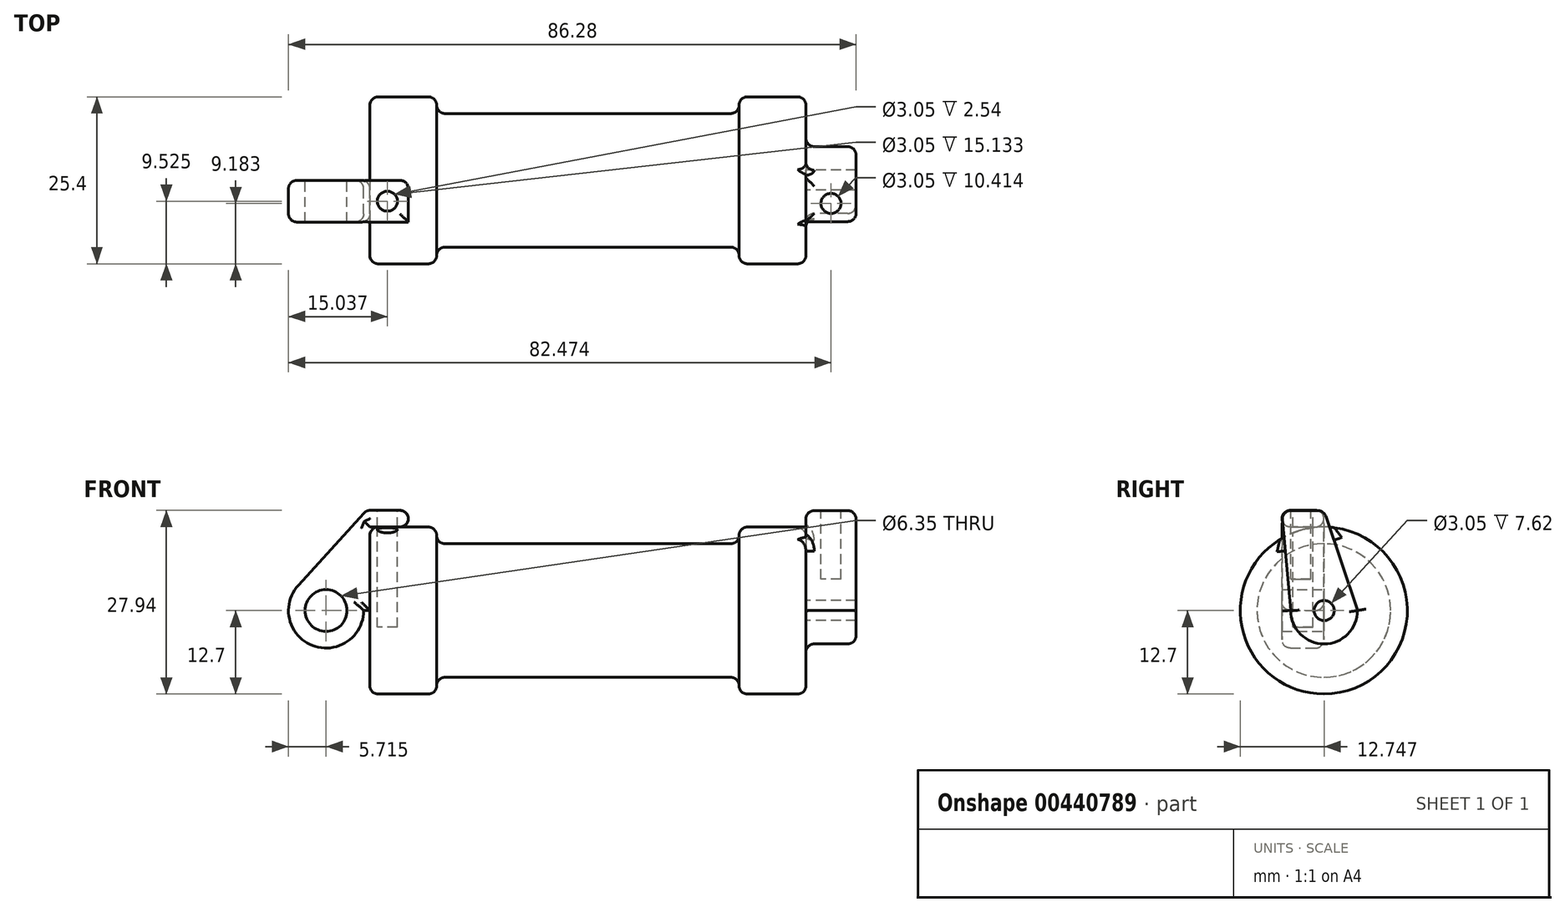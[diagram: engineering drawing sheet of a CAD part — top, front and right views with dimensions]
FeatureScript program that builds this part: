
annotation { "Feature Type Name" : "Feature", "Feature Type Description" : "" }
export const myFeature = defineFeature(function(context is Context, id is Id, definition is map)
    precondition{}
    {
        {
            var Q0;
            Q0=qCreatedBy(makeId("Front.planeOp"),FACE);
            var sketch = newSketch(context, id + "F0", { "sketchPlane" : qUnion([Q0])});
            skLineSegment(sketch, "E0", {"start": v(0, 0) * mm, "end": v(0, 12.7) * mm});
            skLineSegment(sketch, "E1", {"start": v(0, 12.7) * mm, "end": v(10.16, 12.7) * mm});
            skLineSegment(sketch, "E2", {"start": v(10.16, 12.7) * mm, "end": v(10.16, 10.16) * mm});
            skLineSegment(sketch, "E3", {"start": v(10.16, 10.16) * mm, "end": v(56.13, 10.16) * mm});
            skLineSegment(sketch, "E4", {"start": v(56.13, 10.16) * mm, "end": v(56.13, 12.7) * mm});
            skLineSegment(sketch, "E5", {"start": v(56.13, 12.7) * mm, "end": v(66.3, 12.7) * mm});
            skLineSegment(sketch, "E6", {"start": v(66.3, 12.7) * mm, "end": v(66.3, 0) * mm});
            skLineSegment(sketch, "E7", {"start": v(66.3, 0) * mm, "end": v(0, 0) * mm});
            skLineSegment(sketch, "E8", {"start": v(5.84, 15.24) * mm, "end": v(-0.5, 15.24) * mm});
            skLineSegment(sketch, "E9", {"start": v(-0.5, 15.24) * mm, "end": v(-10.88, 3.85) * mm});
            skLineSegment(sketch, "E10", {"start": v(0, 0) * mm, "end": v(-6.65, 0) * mm});
            skCircle(sketch, "E11", {"center": v(-6.65, 0) * mm, "radius": 5.72 * mm});
            skCircle(sketch, "E12", {"center": v(-6.65, 0) * mm, "radius": 3.18 * mm});
            skLineSegment(sketch, "E13", {"start": v(5.84, 15.24) * mm, "end": v(5.84, -9.4) * mm});
            skLineSegment(sketch, "E14", {"start": v(5.84, -9.4) * mm, "end": v(-8.18, -5.5) * mm});
            skSolve(sketch);
        }
        {
            var Q0;
            {var subQ0=sQuery(id+"F0.wireOp",EDGE,"E2");Q0=makeQuery(id+"F0.imprint","IMPRINT",FACE,{"disambiguationData":[TD([[makeQuery(id+"F0.imprint","IMPRINT",EDGE,{"derivedFrom":subQ0}),-1.0]])]});}
            var Q1;
            {var subQ0=sQuery(id+"F0.wireOp",EDGE,"E0");Q1=makeQuery(id+"F0.imprint","IMPRINT",FACE,{"disambiguationData":[TD([[makeQuery(id+"F0.imprint","IMPRINT",EDGE,{"derivedFrom":subQ0}),-1.0]])]});}
            var Q2;
            Q2=sQuery(id+"F0.wireOp",EDGE,"E7");
            revolve(context, id + "F1", {"entities" : qUnion([Q0, Q1]), "axis" : qUnion([Q2]), "revolveType" : RevolveType.FULL});
        }
        {
            var Q0;
            {var subQ1=sQuery(id+"F0.wireOp",EDGE,"E0");Q0=makeQuery(id+"F0.imprint","IMPRINT",FACE,{"disambiguationData":[TD([[makeQuery(id+"F0.imprint","IMPRINT",EDGE,{"derivedFrom":subQ1}),1.0]])]});}
            var Q1;
            {var subQ5=sQuery(id+"F0.wireOp",EDGE,"E12");Q1=makeQuery(id+"F0.imprint","IMPRINT",FACE,{"disambiguationData":[TD([[makeQuery(id+"F0.imprint","IMPRINT",EDGE,{"derivedFrom":subQ5}),-1.0]])]});}
            extrude(context, id + "F2", {"entities" : qUnion([Q0, Q1]), "depth" : 6.35 * mm});
        }
        {
            var Q0;
            Q0=makeQuery(id+"F1.opRevolve","SWEPT_FACE",FACE,{"disambiguationData":[OSD([sQuery(id+"F0.wireOp",EDGE,"E6")])]});
            var sketch = newSketch(context, id + "F3", { "sketchPlane" : qUnion([Q0])});
            skCircle(sketch, "E15", {"center": v(0.05, 0) * mm, "radius": 1.52 * mm});
            skCircle(sketch, "E16", {"center": v(0.05, 0) * mm, "radius": 5.08 * mm});
            skPoint(sketch, "E17", {"position": v(5.13, 0) * mm});
            skPoint(sketch, "E18", {"position": v(-5.03, 0) * mm});
            skLineSegment(sketch, "E19", {"start": v(-5.03, 0) * mm, "end": v(-6.4, 15.2) * mm});
            skLineSegment(sketch, "E20", {"start": v(-6.4, 15.2) * mm, "end": v(0.01, 15.2) * mm});
            skLineSegment(sketch, "E21", {"start": v(0.01, 15.2) * mm, "end": v(5.13, 0) * mm});
            skSolve(sketch);
        }
        {
            var Q0;
            {var subQ0=sQuery(id+"F3.wireOp",EDGE,"E19");var subQ1=sQuery(id+"F3.wireOp",EDGE,"E16");var subQ2=makeQuery(id+"F3.imprint","INTERSECT",VERTEX,{"derivedFrom":[subQ1,subQ0]});Q0=makeQuery(id+"F3.imprint","IMPRINT",FACE,{"disambiguationData":[TD([[makeQuery(id+"F3.imprint","IMPRINT",EDGE,{"disambiguationData":[TD([[subQ2,1.0]])],"derivedFrom":subQ1}),-1.0]])]});}
            var Q1;
            {var subQ0=sQuery(id+"F3.wireOp",EDGE,"E20");Q1=makeQuery(id+"F3.imprint","IMPRINT",FACE,{"disambiguationData":[TD([[makeQuery(id+"F3.imprint","IMPRINT",EDGE,{"derivedFrom":subQ0}),-1.0]])]});}
            var Q2;
            Q2=makeQuery(id+"F3.imprint","IMPRINT",FACE,{"disambiguationData":[TD([[makeQuery(id+"F3.imprint","IMPRINT",EDGE,{"derivedFrom":sQuery(id+"F3.wireOp",EDGE,"E15")}),-1.0]])]});
            extrude(context, id + "F4", {"entities" : qUnion([Q0, Q1, Q2]), "operationType" : NewBodyOperationType.ADD, "depth" : 7.62 * mm});
        }
        {
            var Q0;
            Q0=makeQuery(id+"F4.boolean.opBoolean","SPLIT",FACE,{"disambiguationData":[TD([makeQuery(id+"F4.opExtrude","SWEPT_FACE",FACE,{"disambiguationData":[OSD([sQuery(id+"F3.wireOp",EDGE,"E15")])]})])],"derivedFrom":makeQuery(id+"F1.opRevolve","SWEPT_FACE",FACE,{"disambiguationData":[OSD([sQuery(id+"F0.wireOp",EDGE,"E6")])]})});
            var Q1;
            Q1=makeQuery(id+"F1.opRevolve","SWEPT_FACE",FACE,{"disambiguationData":[OSD([sQuery(id+"F0.wireOp",EDGE,"E2")])]});
            extrude(context, id + "F5", {"entities" : qUnion([Q0]), "operationType" : NewBodyOperationType.ADD, "endBound" : BoundingType.UP_TO_SURFACE, "oppositeDirection" : true, "endBoundEntityFace" : qUnion([Q1]), "depth" : 25.4 * mm});
        }
        {
            var Q0;
            Q0=makeQuery(id+"F2.opExtrude","SWEPT_FACE",FACE,{"disambiguationData":[OSD([sQuery(id+"F0.wireOp",EDGE,"E8")])]});
            var sketch = newSketch(context, id + "F6", { "sketchPlane" : qUnion([Q0])});
            skCircle(sketch, "E22", {"center": v(2.67, -3.18) * mm, "radius": 1.52 * mm});
            skCircle(sketch, "E23", {"center": v(69.7, -3.25) * mm, "radius": 1.52 * mm});
            skPoint(sketch, "E24", {"position": v(2.67, 0) * mm});
            skPoint(sketch, "E25", {"position": v(2.67, -6.35) * mm});
            skPoint(sketch, "E26", {"position": v(69.67, -6.42) * mm});
            skPoint(sketch, "E27", {"position": v(69.72, -0.08) * mm});
            skSolve(sketch);
        }
        {
            var Q0;
            Q0=makeQuery(id+"F6.imprint","IMPRINT",FACE,{"disambiguationData":[TD([[makeQuery(id+"F6.imprint","IMPRINT",EDGE,{"derivedFrom":sQuery(id+"F6.wireOp",EDGE,"E22")}),1.0]])]});
            extrude(context, id + "F7", {"entities" : qUnion([Q0]), "operationType" : NewBodyOperationType.REMOVE, "oppositeDirection" : true, "depth" : 17.78 * mm});
        }
        {
            var Q0;
            Q0=makeQuery(id+"F4.opExtrude","SWEPT_FACE",FACE,{"disambiguationData":[OSD([sQuery(id+"F3.wireOp",EDGE,"E20")])]});
            var sketch = newSketch(context, id + "F8", { "sketchPlane" : qUnion([Q0])});
            skCircle(sketch, "E28", {"center": v(70.1, -3.52) * mm, "radius": 1.52 * mm});
            skPoint(sketch, "E29", {"position": v(70.1, -6.4) * mm});
            skLineSegment(sketch, "E30", {"start": v(70.1, -6.4) * mm, "end": v(70.1, 0.01) * mm});
            skSolve(sketch);
        }
        {
            var Q0;
            {var subQ0=sQuery(id+"F8.wireOp",EDGE,"E30");var subQ1=sQuery(id+"F8.wireOp",EDGE,"E28");var subQ2=makeQuery(id+"F8.imprint","INTERSECT",VERTEX,{"disambiguationData":[OD(0.0)],"derivedFrom":[subQ1,subQ0]});Q0=makeQuery(id+"F8.imprint","IMPRINT",FACE,{"disambiguationData":[TD([[makeQuery(id+"F8.imprint","IMPRINT",EDGE,{"disambiguationData":[TD([[subQ2,-1.0]])],"derivedFrom":subQ1}),1.0]])]});}
            var Q1;
            {var subQ0=sQuery(id+"F8.wireOp",EDGE,"E30");var subQ1=sQuery(id+"F8.wireOp",EDGE,"E28");var subQ2=makeQuery(id+"F8.imprint","INTERSECT",VERTEX,{"disambiguationData":[OD(0.0)],"derivedFrom":[subQ1,subQ0]});Q1=makeQuery(id+"F8.imprint","IMPRINT",FACE,{"disambiguationData":[TD([[makeQuery(id+"F8.imprint","IMPRINT",EDGE,{"disambiguationData":[TD([[subQ2,1.0]])],"derivedFrom":subQ1}),1.0]])]});}
            extrude(context, id + "F9", {"entities" : qUnion([Q0, Q1]), "operationType" : NewBodyOperationType.REMOVE, "oppositeDirection" : true, "depth" : 10.4 * mm});
        }
        {
            var Q0;
            {var subQ0=sQuery(id+"F0.wireOp",EDGE,"E5");var subQ1=sQuery(id+"F0.wireOp",EDGE,"E6");Q0=makeQuery(id+"F4.boolean.opBoolean","SPLIT",EDGE,{"disambiguationData":[topologyDisambiguationEdgeConnected([makeQuery(id+"F1.opRevolve","SWEPT_FACE",FACE,{"disambiguationData":[OSD([subQ1])]})])],"derivedFrom":makeQuery(id+"F1.opRevolve","SWEPT_EDGE",EDGE,{"disambiguationData":[OSD([subQ0,subQ1])]})});}
            var Q1;
            Q1=makeQuery(id+"F1.opRevolve","SWEPT_EDGE",EDGE,{"disambiguationData":[OSD([sQuery(id+"F0.wireOp",EDGE,"E4"),sQuery(id+"F0.wireOp",EDGE,"E5")])]});
            var Q2;
            Q2=makeQuery(id+"F1.opRevolve","SWEPT_EDGE",EDGE,{"disambiguationData":[OSD([sQuery(id+"F0.wireOp",EDGE,"E1"),sQuery(id+"F0.wireOp",EDGE,"E2")])]});
            var Q3;
            Q3=makeQuery(id+"F1.opRevolve","SWEPT_EDGE",EDGE,{"disambiguationData":[OSD([sQuery(id+"F0.wireOp",EDGE,"E0"),sQuery(id+"F0.wireOp",EDGE,"E1")])]});
            var Q4;
            Q4=makeQuery(id+"F1.opRevolve","SWEPT_EDGE",EDGE,{"disambiguationData":[OSD([sQuery(id+"F0.wireOp",EDGE,"E2"),sQuery(id+"F0.wireOp",EDGE,"E3")])]});
            var Q5;
            Q5=makeQuery(id+"F1.opRevolve","SWEPT_EDGE",EDGE,{"disambiguationData":[OSD([sQuery(id+"F0.wireOp",EDGE,"E3"),sQuery(id+"F0.wireOp",EDGE,"E4")])]});
            fillet(context, id + "F10", {"entities" : qUnion([Q0, Q1, Q2, Q3, Q4, Q5]), "radius" : 1.27 * mm, "tangentPropagation" : true, "allowEdgeOverflow" : false});
        }
        {
            var Q0;
            {var subQ0=sQuery(id+"F3.wireOp",EDGE,"E19");Q0=makeQuery(id+"F4.boolean.opBoolean","SPLIT",EDGE,{"disambiguationData":[topologyDisambiguationEdgeConnected([makeQuery(id+"F1.opRevolve","SWEPT_FACE",FACE,{"disambiguationData":[OSD([sQuery(id+"F0.wireOp",EDGE,"E6")])]})])],"derivedFrom":makeQuery(id+"F4.opExtrude","CAP_EDGE",EDGE,{"disambiguationData":[OSD([subQ0])],"isStart":true})});}
            var Q1;
            Q1=makeQuery(id+"F4.opExtrude","CAP_EDGE",EDGE,{"disambiguationData":[OSD([sQuery(id+"F3.wireOp",EDGE,"E16")])],"isStart":true});
            var Q2;
            Q2=makeQuery(id+"F4.opExtrude","SWEPT_EDGE",EDGE,{"disambiguationData":[OSD([sQuery(id+"F3.wireOp",EDGE,"E19"),sQuery(id+"F3.wireOp",EDGE,"E20")])]});
            var Q3;
            Q3=makeQuery(id+"F4.opExtrude","CAP_EDGE",EDGE,{"disambiguationData":[OSD([sQuery(id+"F3.wireOp",EDGE,"E20")])],"isStart":false});
            var Q4;
            Q4=makeQuery(id+"F4.opExtrude","CAP_EDGE",EDGE,{"disambiguationData":[OSD([sQuery(id+"F3.wireOp",EDGE,"E20")])],"isStart":true});
            var Q5;
            Q5=makeQuery(id+"F4.opExtrude","SWEPT_EDGE",EDGE,{"disambiguationData":[OSD([sQuery(id+"F3.wireOp",EDGE,"E20"),sQuery(id+"F3.wireOp",EDGE,"E21")])]});
            var Q6;
            {var subQ0=sQuery(id+"F3.wireOp",EDGE,"E21");Q6=makeQuery(id+"F4.boolean.opBoolean","SPLIT",EDGE,{"disambiguationData":[topologyDisambiguationEdgeConnected([makeQuery(id+"F1.opRevolve","SWEPT_FACE",FACE,{"disambiguationData":[OSD([sQuery(id+"F0.wireOp",EDGE,"E6")])]})])],"derivedFrom":makeQuery(id+"F4.opExtrude","CAP_EDGE",EDGE,{"disambiguationData":[OSD([subQ0])],"isStart":true})});}
            var Q7;
            Q7=makeQuery(id+"F4.opExtrude","CAP_EDGE",EDGE,{"disambiguationData":[OSD([sQuery(id+"F3.wireOp",EDGE,"E21")])],"isStart":false});
            var Q8;
            Q8=makeQuery(id+"F4.opExtrude","CAP_EDGE",EDGE,{"disambiguationData":[OSD([sQuery(id+"F3.wireOp",EDGE,"E19")])],"isStart":false});
            var Q9;
            Q9=makeQuery(id+"F4.opExtrude","CAP_EDGE",EDGE,{"disambiguationData":[OSD([sQuery(id+"F3.wireOp",EDGE,"E16")])],"isStart":false});
            fillet(context, id + "F11", {"entities" : qUnion([Q0, Q1, Q2, Q3, Q4, Q5, Q6, Q7, Q8, Q9]), "radius" : 1.27 * mm, "tangentPropagation" : true, "allowEdgeOverflow" : false});
        }
        {
            var Q0;
            Q0=makeQuery(id+"F2.opExtrude","CAP_EDGE",EDGE,{"disambiguationData":[OSD([sQuery(id+"F0.wireOp",EDGE,"E13")])],"isStart":true});
            var Q1;
            Q1=makeQuery(id+"F2.opExtrude","SWEPT_EDGE",EDGE,{"disambiguationData":[OSD([sQuery(id+"F0.wireOp",EDGE,"E8"),sQuery(id+"F0.wireOp",EDGE,"E13")])]});
            var Q2;
            Q2=makeQuery(id+"F2.opExtrude","SWEPT_EDGE",EDGE,{"disambiguationData":[OSD([sQuery(id+"F0.wireOp",EDGE,"E1"),sQuery(id+"F0.wireOp",EDGE,"E13")])]});
            var Q3;
            Q3=makeQuery(id+"F2.opExtrude","CAP_EDGE",EDGE,{"disambiguationData":[OSD([sQuery(id+"F0.wireOp",EDGE,"E9")])],"isStart":false});
            var Q4;
            Q4=makeQuery(id+"F2.opExtrude","CAP_EDGE",EDGE,{"disambiguationData":[OSD([sQuery(id+"F0.wireOp",EDGE,"E8")])],"isStart":true});
            var Q5;
            Q5=makeQuery(id+"F2.opExtrude","CAP_EDGE",EDGE,{"disambiguationData":[OSD([sQuery(id+"F0.wireOp",EDGE,"E9")])],"isStart":true});
            var Q6;
            Q6=makeQuery(id+"F2.opExtrude","SWEPT_EDGE",EDGE,{"disambiguationData":[OSD([sQuery(id+"F0.wireOp",EDGE,"E8"),sQuery(id+"F0.wireOp",EDGE,"E9")])]});
            var Q7;
            Q7=makeQuery(id+"F2.opExtrude","CAP_EDGE",EDGE,{"disambiguationData":[OSD([sQuery(id+"F0.wireOp",EDGE,"E8")])],"isStart":false});
            var Q8;
            Q8=makeQuery(id+"F2.opExtrude","CAP_EDGE",EDGE,{"disambiguationData":[OSD([sQuery(id+"F0.wireOp",EDGE,"E11")])],"isStart":true});
            var Q9;
            Q9=makeQuery(id+"F2.opExtrude","CAP_EDGE",EDGE,{"disambiguationData":[OSD([sQuery(id+"F0.wireOp",EDGE,"E10")])],"isStart":true});
            var Q10;
            Q10=makeQuery(id+"F2.opExtrude","CAP_EDGE",EDGE,{"disambiguationData":[OSD([sQuery(id+"F0.wireOp",EDGE,"E0")])],"isStart":true});
            var Q11;
            Q11=makeQuery(id+"F2.opExtrude","CAP_EDGE",EDGE,{"disambiguationData":[OSD([sQuery(id+"F0.wireOp",EDGE,"E1")])],"isStart":true});
            var Q12;
            Q12=makeQuery(id+"F2.opExtrude","CAP_EDGE",EDGE,{"disambiguationData":[OSD([sQuery(id+"F0.wireOp",EDGE,"E11")])],"isStart":false});
            var Q13;
            Q13=makeQuery(id+"F2.opExtrude","CAP_EDGE",EDGE,{"disambiguationData":[OSD([sQuery(id+"F0.wireOp",EDGE,"E10")])],"isStart":false});
            var Q14;
            Q14=makeQuery(id+"F2.opExtrude","CAP_EDGE",EDGE,{"disambiguationData":[OSD([sQuery(id+"F0.wireOp",EDGE,"E0")])],"isStart":false});
            var Q15;
            Q15=makeQuery(id+"F2.opExtrude","CAP_EDGE",EDGE,{"disambiguationData":[OSD([sQuery(id+"F0.wireOp",EDGE,"E1")])],"isStart":false});
            fillet(context, id + "F12", {"entities" : qUnion([Q0, Q1, Q2, Q3, Q4, Q5, Q6, Q7, Q8, Q9, Q10, Q11, Q12, Q13, Q14, Q15]), "radius" : 1.27 * mm, "tangentPropagation" : true, "allowEdgeOverflow" : false});
        }
    });
